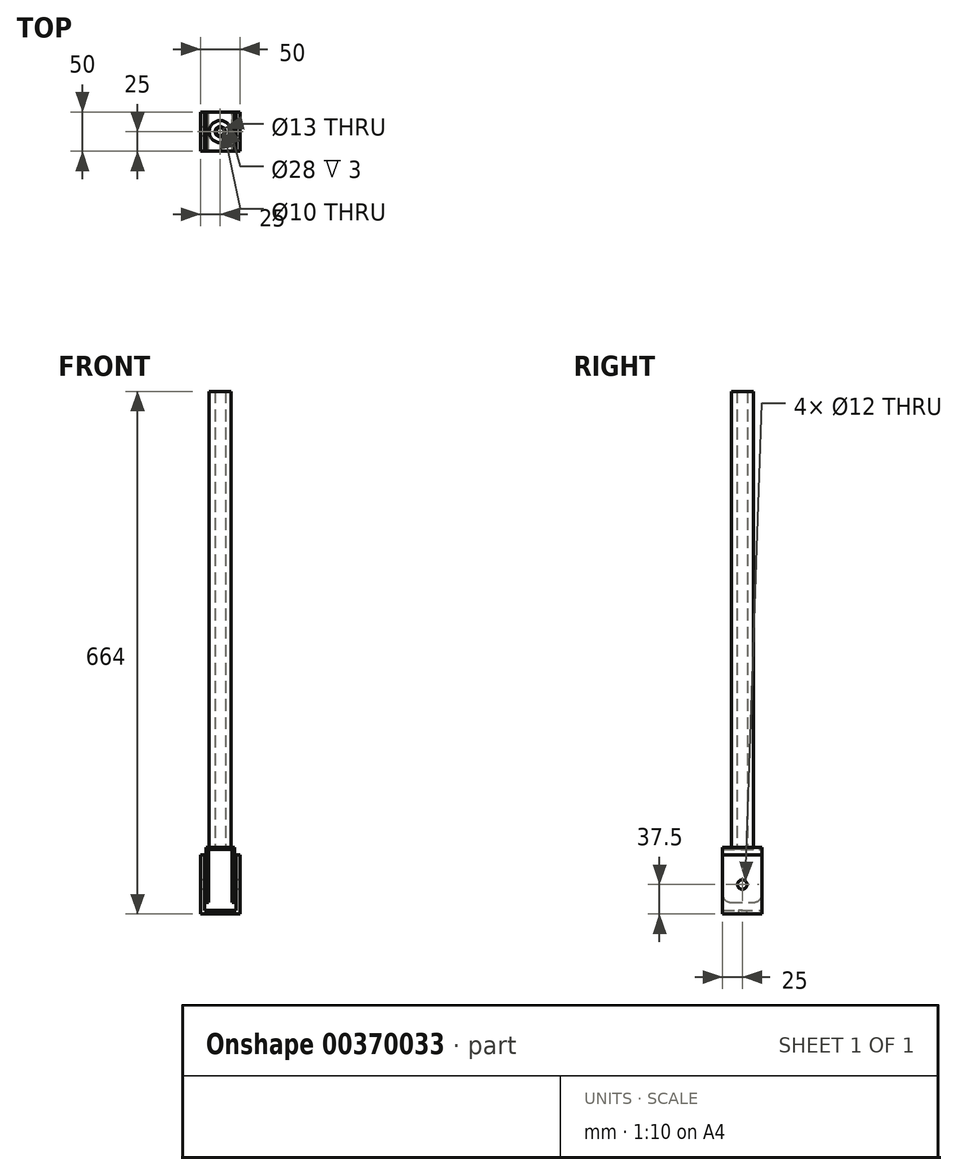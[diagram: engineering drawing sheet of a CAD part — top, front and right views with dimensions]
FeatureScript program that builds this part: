
annotation { "Feature Type Name" : "Feature", "Feature Type Description" : "" }
export const myFeature = defineFeature(function(context is Context, id is Id, definition is map)
    precondition{}
    {
        {
            var Q0;
            Q0=qCreatedBy(makeId("Front.planeOp"),FACE);
            var sketch = newSketch(context, id + "F0", { "sketchPlane" : qUnion([Q0])});
            skLineSegment(sketch, "E0", {"start": v(0, 0) * mm, "end": v(0, 70) * mm});
            skLineSegment(sketch, "E1", {"start": v(0, 0) * mm, "end": v(40, 0) * mm});
            skLineSegment(sketch, "E2", {"start": v(40, 0) * mm, "end": v(40, 70) * mm});
            skLineSegment(sketch, "E3", {"start": v(40, 70) * mm, "end": v(45, 70) * mm});
            skLineSegment(sketch, "E4", {"start": v(45, 70) * mm, "end": v(45, -5) * mm});
            skLineSegment(sketch, "E5", {"start": v(45, -5) * mm, "end": v(-5, -5) * mm});
            skLineSegment(sketch, "E6", {"start": v(-5, -5) * mm, "end": v(-5, 70) * mm});
            skLineSegment(sketch, "E7", {"start": v(-5, 70) * mm, "end": v(0, 70) * mm});
            skSolve(sketch);
        }
        {
            var Q0;
            Q0 = qSketchRegion(id + "F0", true);
            extrude(context, id + "F1", {"entities" : qUnion([Q0]), "depth" : 50 * mm});
        }
        {
            var Q0;
            Q0=makeQuery(id+"F1.opExtrude","SWEPT_FACE",FACE,{"disambiguationData":[OSD([sQuery(id+"F0.wireOp",EDGE,"E5")])]});
            var sketch = newSketch(context, id + "F2", { "sketchPlane" : qUnion([Q0])});
            skPoint(sketch, "E8", {"position": v(20, 25) * mm});
            skPoint(sketch, "E8.positionSnap0", {"position": v(-5, 25) * mm});
            skPoint(sketch, "E8.positionSnap1", {"position": v(20, 0) * mm});
            skCircle(sketch, "E9", {"center": v(20, 25) * mm, "radius": 5 * mm});
            skSolve(sketch);
        }
        {
            var Q0;
            Q0 = qSketchRegion(id + "F2", true);
            extrude(context, id + "F3", {"entities" : qUnion([Q0]), "operationType" : NewBodyOperationType.REMOVE, "oppositeDirection" : true, "depth" : 25 * mm});
        }
        {
            var Q0;
            Q0=makeQuery(id+"F1.opExtrude","SWEPT_FACE",FACE,{"disambiguationData":[OSD([sQuery(id+"F0.wireOp",EDGE,"E6")])]});
            var sketch = newSketch(context, id + "F4", { "sketchPlane" : qUnion([Q0])});
            skPoint(sketch, "E10", {"position": v(25, 32.5) * mm});
            skPoint(sketch, "E10.positionSnap0", {"position": v(50, 32.5) * mm});
            skPoint(sketch, "E10.positionSnap1", {"position": v(25, 70) * mm});
            skCircle(sketch, "E11", {"center": v(25, 32.5) * mm, "radius": 6 * mm});
            skSolve(sketch);
        }
        {
            var Q0;
            Q0 = qSketchRegion(id + "F4", true);
            extrude(context, id + "F5", {"entities" : qUnion([Q0]), "operationType" : NewBodyOperationType.REMOVE, "oppositeDirection" : true, "depth" : 50 * mm});
        }
        {
            var Q0;
            Q0=qCreatedBy(makeId("Front.planeOp"),FACE);
            var sketch = newSketch(context, id + "F6", { "sketchPlane" : qUnion([Q0])});
            skPoint(sketch, "E12", {"position": v(0, 0) * mm});
            skPoint(sketch, "E13", {"position": v(2, 0) * mm});
            skPoint(sketch, "E14", {"position": v(2, 10) * mm});
            skLineSegment(sketch, "E15", {"start": v(2, 10) * mm, "end": v(2, 80) * mm});
            skLineSegment(sketch, "E16", {"start": v(38, 10) * mm, "end": v(38, 80) * mm});
            skLineSegment(sketch, "E17", {"start": v(38, 77) * mm, "end": v(2, 77) * mm});
            skLineSegment(sketch, "E18", {"start": v(2, 80) * mm, "end": v(38, 80) * mm});
            skPoint(sketch, "E19", {"position": v(35, 80) * mm});
            skPoint(sketch, "E20", {"position": v(5, 80) * mm});
            skLineSegment(sketch, "E21", {"start": v(5, 80) * mm, "end": v(5, 10) * mm});
            skLineSegment(sketch, "E22", {"start": v(5, 10) * mm, "end": v(2, 10) * mm});
            skLineSegment(sketch, "E23", {"start": v(38, 10) * mm, "end": v(35, 10) * mm});
            skLineSegment(sketch, "E24", {"start": v(35, 10) * mm, "end": v(35, 80) * mm});
            skSolve(sketch);
        }
        {
            var Q0;
            Q0 = qSketchRegion(id + "F6", true);
            extrude(context, id + "F7", {"entities" : qUnion([Q0]), "depth" : 50 * mm});
        }
        {
            var Q0;
            Q0=makeQuery(id+"F7.opExtrude","SWEPT_FACE",FACE,{"disambiguationData":[OSD([sQuery(id+"F6.wireOp",EDGE,"E16")])]});
            var sketch = newSketch(context, id + "F8", { "sketchPlane" : qUnion([Q0])});
            skCircle(sketch, "E25.0", {"center": v(-25, 32.5) * mm, "radius": 6 * mm});
            skSolve(sketch);
        }
        {
            var Q0;
            Q0 = qSketchRegion(id + "F8", true);
            extrude(context, id + "F9", {"entities" : qUnion([Q0]), "operationType" : NewBodyOperationType.REMOVE, "oppositeDirection" : true, "depth" : 36 * mm});
        }
        {
            var Q0;
            Q0=makeQuery(id+"F7.opExtrude","SWEPT_FACE",FACE,{"disambiguationData":[OSD([sQuery(id+"F6.wireOp",EDGE,"E18")])]});
            var sketch = newSketch(context, id + "F10", { "sketchPlane" : qUnion([Q0])});
            skPoint(sketch, "E26", {"position": v(20, -25) * mm});
            skPoint(sketch, "E26.positionSnap0", {"position": v(2, -25) * mm});
            skPoint(sketch, "E26.positionSnap1", {"position": v(20, -50) * mm});
            skCircle(sketch, "E27", {"center": v(20, -25) * mm, "radius": 14 * mm});
            skSolve(sketch);
        }
        {
            var Q0;
            Q0 = qSketchRegion(id + "F10", true);
            extrude(context, id + "F11", {"entities" : qUnion([Q0]), "operationType" : NewBodyOperationType.REMOVE, "oppositeDirection" : true, "depth" : 5 * mm});
        }
        {
            var Q0;
            Q0=qCreatedBy(makeId("Right.planeOp"),FACE);
            cPlane(context, id + "F12", {"entities" : qUnion([Q0]), "cplaneType" : CPlaneType.OFFSET, "offset" : 20 * mm, "width" : 150 * mm, "height" : 150 * mm});
        }
        {
            var Q0;
            Q0=qCreatedBy(id+"F12.planeOp",FACE);
            var sketch = newSketch(context, id + "F13", { "sketchPlane" : qUnion([Q0])});
            skPoint(sketch, "E28", {"position": v(-25, 80) * mm});
            skLineSegment(sketch, "E29", {"start": v(-25, 80) * mm, "end": v(-25, 659) * mm});
            skLineSegment(sketch, "E30", {"start": v(-25, 659) * mm, "end": v(-39, 659) * mm});
            skLineSegment(sketch, "E31", {"start": v(-39, 659) * mm, "end": v(-39, 80) * mm});
            skLineSegment(sketch, "E32", {"start": v(-39, 80) * mm, "end": v(-25, 80) * mm});
            skPoint(sketch, "E33", {"position": v(-31.5, 659) * mm});
            skLineSegment(sketch, "E34", {"start": v(-31.5, 659) * mm, "end": v(-31.5, 80) * mm});
            skSolve(sketch);
        }
        {
            var Q0;
            {var subQ0=sQuery(id+"F13.wireOp",EDGE,"E31");Q0=makeQuery(id+"F13.imprint","IMPRINT",FACE,{"disambiguationData":[TD([[makeQuery(id+"F13.imprint","IMPRINT",EDGE,{"derivedFrom":subQ0}),1.0]])]});}
            var Q1;
            Q1=sQuery(id+"F13.wireOp",EDGE,"E29");
            revolve(context, id + "F14", {"entities" : qUnion([Q0]), "axis" : qUnion([Q1]), "revolveType" : RevolveType.FULL});
        }
        {
            var Q0;
            Q0=makeQuery(id+"F7.opExtrude","CAP_EDGE",EDGE,{"disambiguationData":[OSD([sQuery(id+"F6.wireOp",EDGE,"E23")])],"isStart":false});
            var Q1;
            Q1=makeQuery(id+"F7.opExtrude","CAP_EDGE",EDGE,{"disambiguationData":[OSD([sQuery(id+"F6.wireOp",EDGE,"E22")])],"isStart":false});
            var Q2;
            Q2=makeQuery(id+"F7.opExtrude","CAP_EDGE",EDGE,{"disambiguationData":[OSD([sQuery(id+"F6.wireOp",EDGE,"E23")])],"isStart":true});
            var Q3;
            Q3=makeQuery(id+"F7.opExtrude","CAP_EDGE",EDGE,{"disambiguationData":[OSD([sQuery(id+"F6.wireOp",EDGE,"E22")])],"isStart":true});
            fillet(context, id + "F15", {"entities" : qUnion([Q0, Q1, Q2, Q3]), "radius" : 10 * mm, "tangentPropagation" : true, "allowEdgeOverflow" : false});
        }
    });
